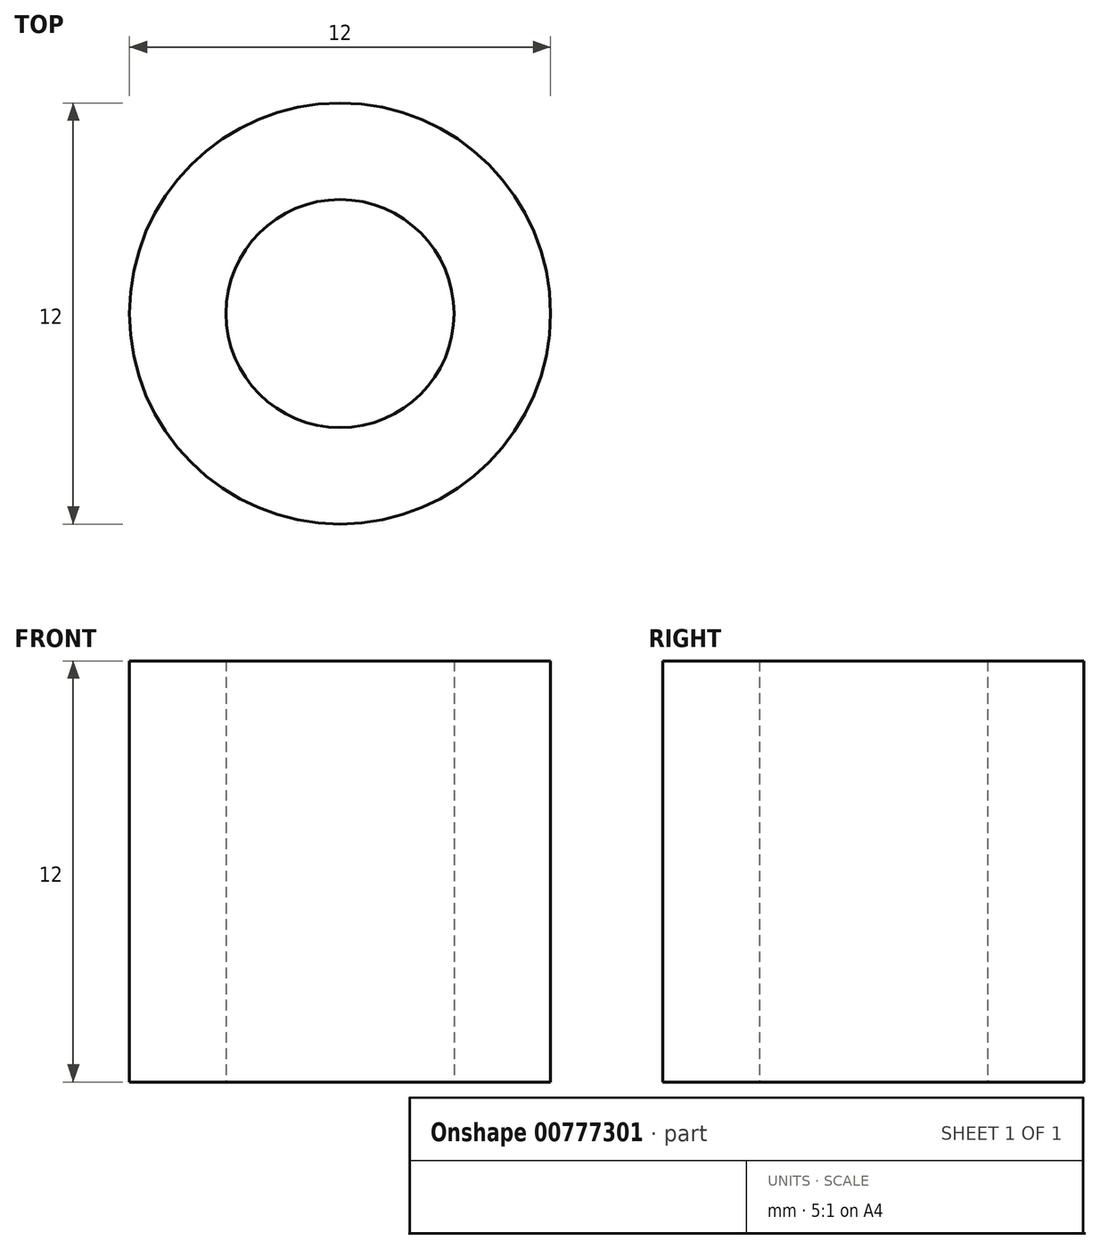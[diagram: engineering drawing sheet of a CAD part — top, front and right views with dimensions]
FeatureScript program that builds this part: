
annotation { "Feature Type Name" : "Feature", "Feature Type Description" : "" }
export const myFeature = defineFeature(function(context is Context, id is Id, definition is map)
    precondition{}
    {
        {
            var Q0;
            Q0=qCreatedBy(makeId("Top.planeOp"),FACE);
            var sketch = newSketch(context, id + "F0", { "sketchPlane" : qUnion([Q0])});
            skCircle(sketch, "E0", {"center": v(0, 0) * mm, "radius": 3.25 * mm});
            skCircle(sketch, "E1", {"center": v(0, 0) * mm, "radius": 6 * mm});
            skSolve(sketch);
        }
        {
            var Q0;
            Q0=makeQuery(id+"F0.imprint","IMPRINT",FACE,{"disambiguationData":[TD([[makeQuery(id+"F0.imprint","IMPRINT",EDGE,{"derivedFrom":sQuery(id+"F0.wireOp",EDGE,"E0")}),-1.0]])]});
            extrude(context, id + "F1", {"entities" : qUnion([Q0]), "depth" : 12 * mm, "offsetDistance" : 25 * mm});
        }
    });
